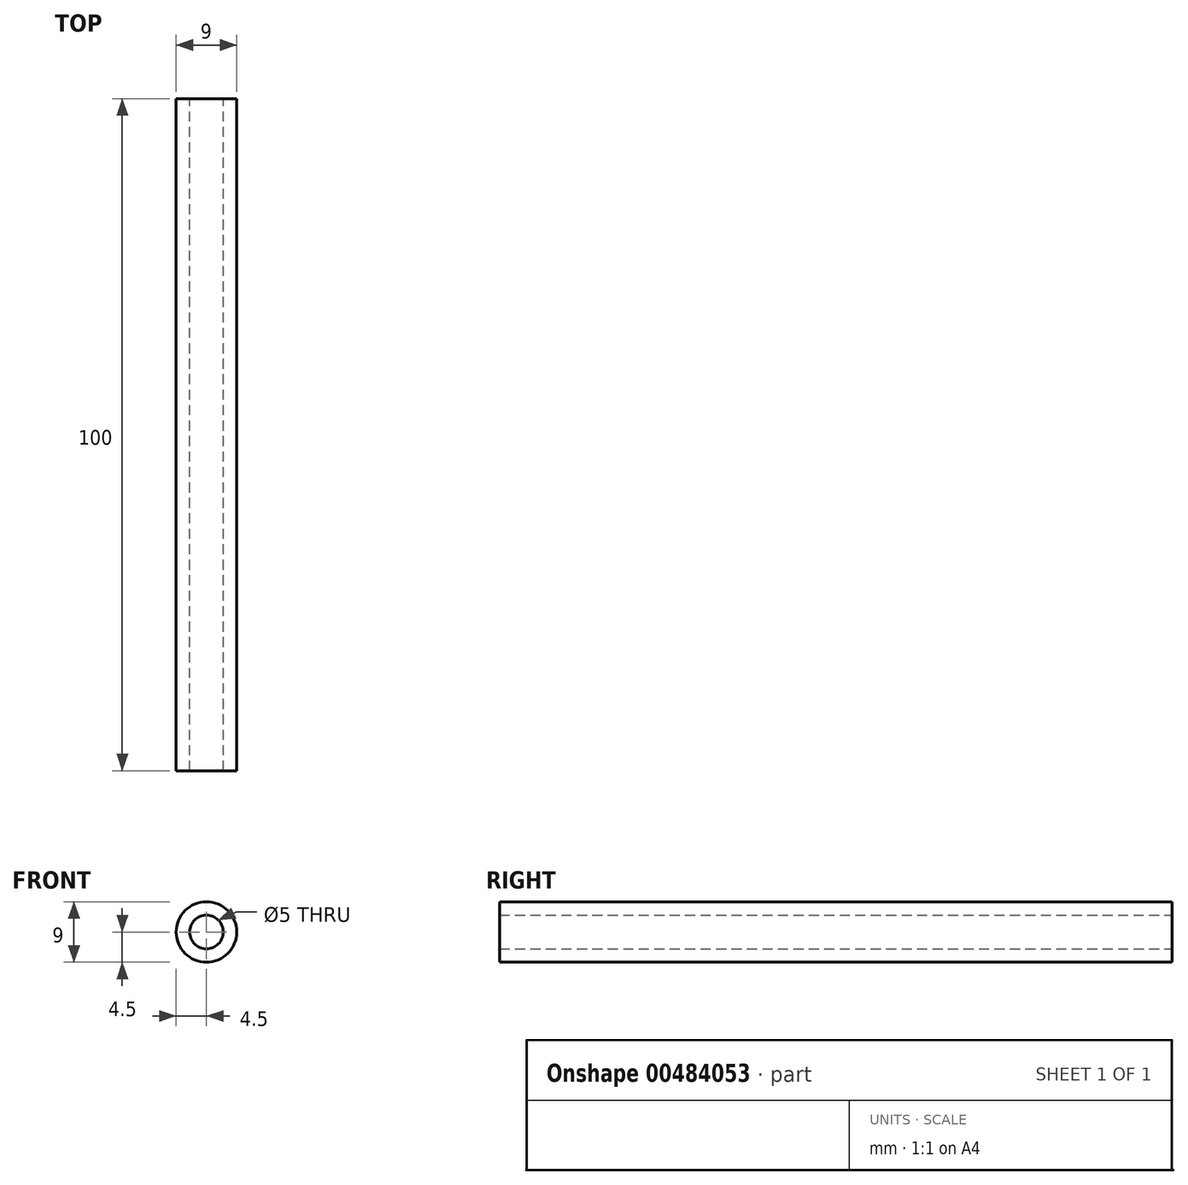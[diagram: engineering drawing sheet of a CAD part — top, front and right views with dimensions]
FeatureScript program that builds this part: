
annotation { "Feature Type Name" : "Feature", "Feature Type Description" : "" }
export const myFeature = defineFeature(function(context is Context, id is Id, definition is map)
    precondition{}
    {
        {
            var Q0;
            Q0=qCreatedBy(makeId("Front.planeOp"),FACE);
            var sketch = newSketch(context, id + "F0", { "sketchPlane" : qUnion([Q0])});
            skCircle(sketch, "E0", {"center": v(0, 0) * mm, "radius": 2.5 * mm});
            skCircle(sketch, "E1", {"center": v(0, 0) * mm, "radius": 4.5 * mm});
            skSolve(sketch);
        }
        {
            var Q0;
            Q0=makeQuery(id+"F0.imprint","IMPRINT",FACE,{"disambiguationData":[TD([[makeQuery(id+"F0.imprint","IMPRINT",EDGE,{"derivedFrom":sQuery(id+"F0.wireOp",EDGE,"E0")}),-1.0]])]});
            extrude(context, id + "F1", {"entities" : qUnion([Q0]), "endBound" : BoundingType.SYMMETRIC, "depth" : 100 * mm});
        }
    });
